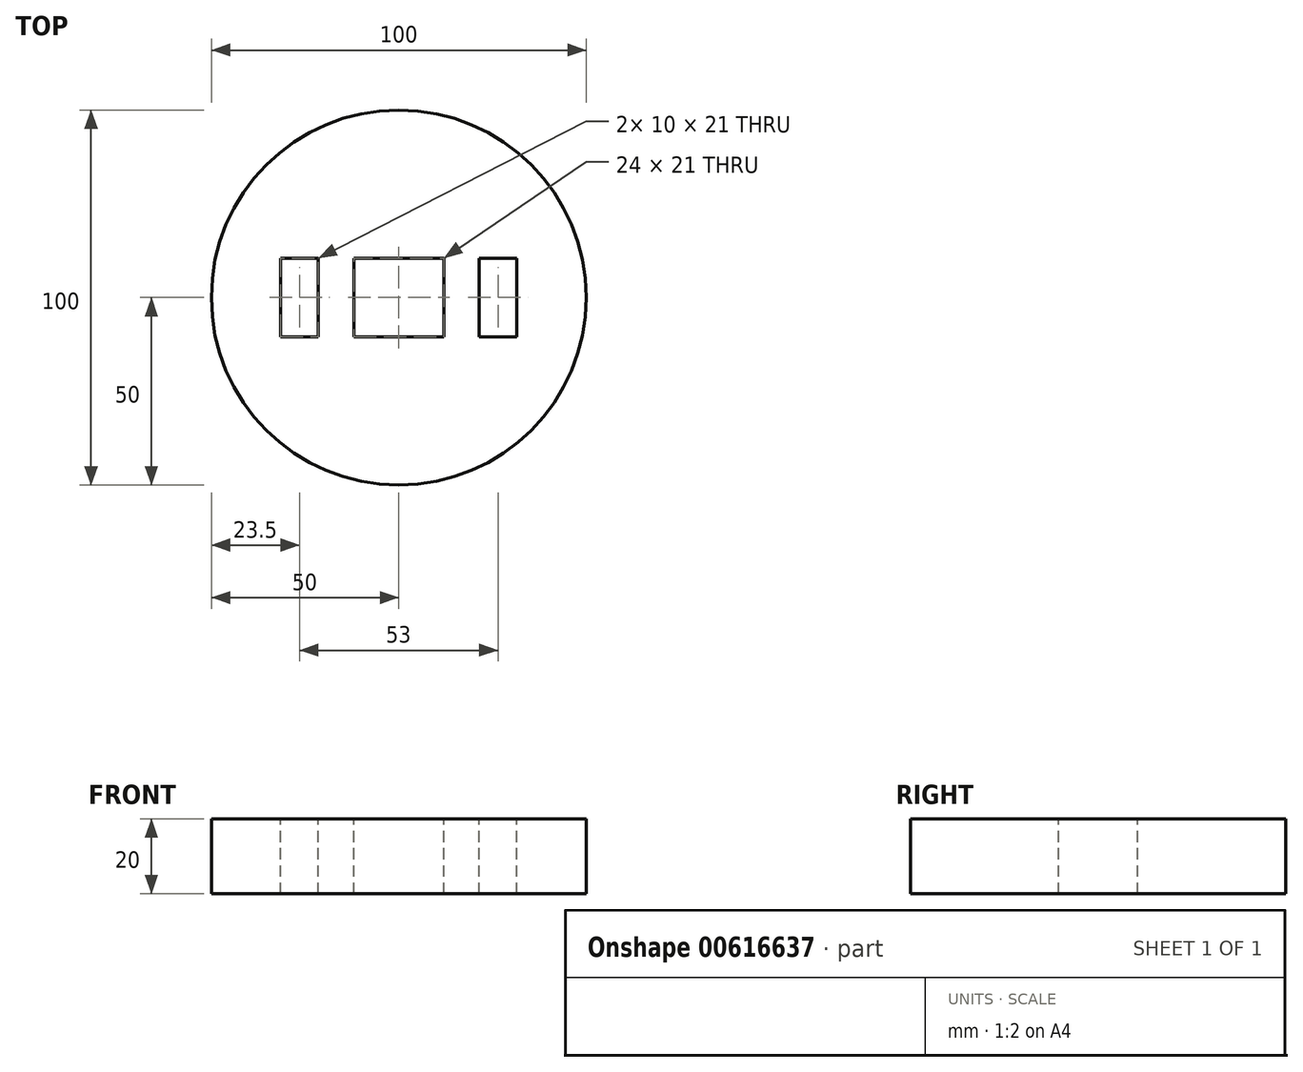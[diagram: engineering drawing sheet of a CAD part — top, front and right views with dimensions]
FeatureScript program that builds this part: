
annotation { "Feature Type Name" : "Feature", "Feature Type Description" : "" }
export const myFeature = defineFeature(function(context is Context, id is Id, definition is map)
    precondition{}
    {
        {
            var Q0;
            Q0=qCreatedBy(makeId("Top.planeOp"),FACE);
            var sketch = newSketch(context, id + "F0", { "sketchPlane" : qUnion([Q0])});
            skCircle(sketch, "E0", {"center": v(0, 0) * mm, "radius": 50 * mm});
            skLineSegment(sketch, "E1.bottom", {"start": v(-31.5, 10.5) * mm, "end": v(-21.5, 10.5) * mm});
            skLineSegment(sketch, "E1.top", {"start": v(-31.5, -10.5) * mm, "end": v(-21.5, -10.5) * mm});
            skLineSegment(sketch, "E1.left", {"start": v(-31.5, 10.5) * mm, "end": v(-31.5, -10.5) * mm});
            skLineSegment(sketch, "E1.right", {"start": v(-21.5, 10.5) * mm, "end": v(-21.5, -10.5) * mm});
            skLineSegment(sketch, "E2.bottom", {"start": v(21.5, 10.5) * mm, "end": v(31.5, 10.5) * mm});
            skLineSegment(sketch, "E2.top", {"start": v(21.5, -10.5) * mm, "end": v(31.5, -10.5) * mm});
            skLineSegment(sketch, "E2.left", {"start": v(21.5, 10.5) * mm, "end": v(21.5, -10.5) * mm});
            skLineSegment(sketch, "E2.right", {"start": v(31.5, 10.5) * mm, "end": v(31.5, -10.5) * mm});
            skLineSegment(sketch, "E3.bottom", {"start": v(-12, 10.5) * mm, "end": v(12, 10.5) * mm});
            skLineSegment(sketch, "E3.top", {"start": v(-12, -10.5) * mm, "end": v(12, -10.5) * mm});
            skLineSegment(sketch, "E3.left", {"start": v(-12, 10.5) * mm, "end": v(-12, -10.5) * mm});
            skLineSegment(sketch, "E3.right", {"start": v(12, 10.5) * mm, "end": v(12, -10.5) * mm});
            skSolve(sketch);
        }
        {
            var Q0;
            Q0 = qSketchRegion(id + "F0", true);
            extrude(context, id + "F1", {"entities" : qUnion([Q0]), "oppositeDirection" : true, "depth" : 20 * mm, "offsetDistance" : 25 * mm});
        }
    });
